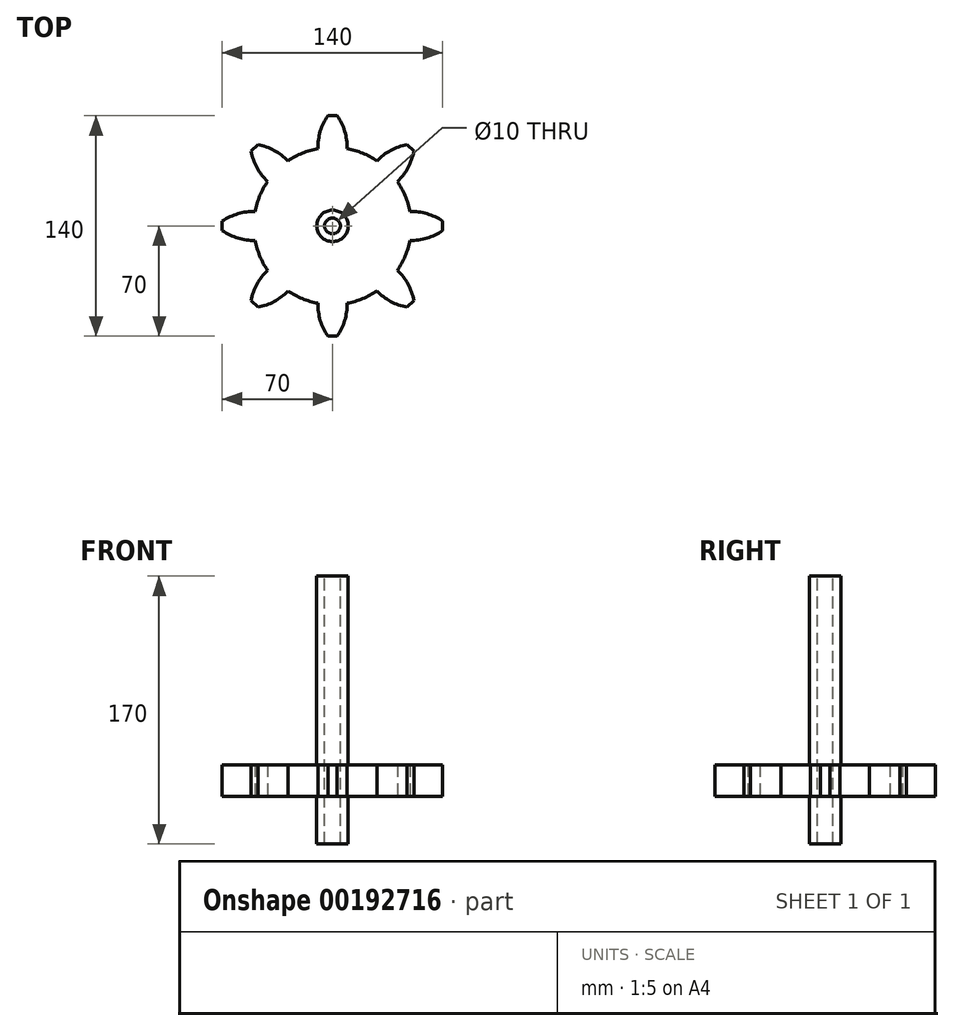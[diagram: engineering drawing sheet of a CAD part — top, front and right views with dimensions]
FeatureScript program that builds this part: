
annotation { "Feature Type Name" : "Feature", "Feature Type Description" : "" }
export const myFeature = defineFeature(function(context is Context, id is Id, definition is map)
    precondition{}
    {
        {
            var Q0;
            Q0=qCreatedBy(makeId("Top.planeOp"),FACE);
            var sketch = newSketch(context, id + "F0", { "sketchPlane" : qUnion([Q0])});
            skCircle(sketch, "E0", {"center": v(0, 0) * mm, "radius": 50 * mm});
            skLineSegment(sketch, "E1", {"start": v(0, 0) * mm, "end": v(0, 50) * mm, "construction": true});
            skLineSegment(sketch, "E2", {"start": v(0, 50) * mm, "end": v(0, 70) * mm});
            skLineSegment(sketch, "E3", {"start": v(0, 70) * mm, "end": v(-3, 70) * mm});
            skArc(sketch, "E4", {"start": v(-3, 70) * mm, "mid": v(-7.76, 60.06) * mm, "end": v(-9.22, 49.14) * mm});
            skLineSegment(sketch, "E5.MirrorCS", {"start": v(0, 70) * mm, "end": v(3, 70) * mm});
            skArc(sketch, "E6.MirrorCS", {"start": v(3, 70) * mm, "mid": v(7.76, 60.06) * mm, "end": v(9.22, 49.14) * mm});
            skArc(sketch, "E7.1.0", {"start": v(-51.62, 47.38) * mm, "mid": v(-47.96, 36.98) * mm, "end": v(-41.27, 28.23) * mm});
            skLineSegment(sketch, "E7.1.1", {"start": v(-49.5, 49.5) * mm, "end": v(-51.62, 47.38) * mm});
            skLineSegment(sketch, "E7.1.2", {"start": v(-49.5, 49.5) * mm, "end": v(-47.38, 51.62) * mm});
            skArc(sketch, "E7.1.3", {"start": v(-47.38, 51.62) * mm, "mid": v(-36.98, 47.96) * mm, "end": v(-28.23, 41.27) * mm});
            skArc(sketch, "E7.2.0", {"start": v(-70, -3) * mm, "mid": v(-60.06, -7.76) * mm, "end": v(-49.14, -9.22) * mm});
            skLineSegment(sketch, "E7.2.1", {"start": v(-70, 0) * mm, "end": v(-70, -3) * mm});
            skLineSegment(sketch, "E7.2.2", {"start": v(-70, 0) * mm, "end": v(-70, 3) * mm});
            skArc(sketch, "E7.2.3", {"start": v(-70, 3) * mm, "mid": v(-60.06, 7.76) * mm, "end": v(-49.14, 9.22) * mm});
            skArc(sketch, "E7.3.0", {"start": v(-47.38, -51.62) * mm, "mid": v(-36.98, -47.96) * mm, "end": v(-28.23, -41.27) * mm});
            skLineSegment(sketch, "E7.3.1", {"start": v(-49.5, -49.5) * mm, "end": v(-47.38, -51.62) * mm});
            skLineSegment(sketch, "E7.3.2", {"start": v(-49.5, -49.5) * mm, "end": v(-51.62, -47.38) * mm});
            skArc(sketch, "E7.3.3", {"start": v(-51.62, -47.38) * mm, "mid": v(-47.96, -36.98) * mm, "end": v(-41.27, -28.23) * mm});
            skArc(sketch, "E7.4.0", {"start": v(3, -70) * mm, "mid": v(7.76, -60.06) * mm, "end": v(9.22, -49.14) * mm});
            skLineSegment(sketch, "E7.4.1", {"start": v(0, -70) * mm, "end": v(3, -70) * mm});
            skLineSegment(sketch, "E7.4.2", {"start": v(0, -70) * mm, "end": v(-3, -70) * mm});
            skArc(sketch, "E7.4.3", {"start": v(-3, -70) * mm, "mid": v(-7.76, -60.06) * mm, "end": v(-9.22, -49.14) * mm});
            skArc(sketch, "E7.5.0", {"start": v(51.62, -47.38) * mm, "mid": v(47.96, -36.98) * mm, "end": v(41.27, -28.23) * mm});
            skLineSegment(sketch, "E7.5.1", {"start": v(49.5, -49.5) * mm, "end": v(51.62, -47.38) * mm});
            skLineSegment(sketch, "E7.5.2", {"start": v(49.5, -49.5) * mm, "end": v(47.38, -51.62) * mm});
            skArc(sketch, "E7.5.3", {"start": v(47.38, -51.62) * mm, "mid": v(36.98, -47.96) * mm, "end": v(28.23, -41.27) * mm});
            skArc(sketch, "E7.6.0", {"start": v(70, 3) * mm, "mid": v(60.06, 7.76) * mm, "end": v(49.14, 9.22) * mm});
            skLineSegment(sketch, "E7.6.1", {"start": v(70, 0) * mm, "end": v(70, 3) * mm});
            skLineSegment(sketch, "E7.6.2", {"start": v(70, 0) * mm, "end": v(70, -3) * mm});
            skArc(sketch, "E7.6.3", {"start": v(70, -3) * mm, "mid": v(60.06, -7.76) * mm, "end": v(49.14, -9.22) * mm});
            skArc(sketch, "E7.7.0", {"start": v(47.38, 51.62) * mm, "mid": v(36.98, 47.96) * mm, "end": v(28.23, 41.27) * mm});
            skLineSegment(sketch, "E7.7.1", {"start": v(49.5, 49.5) * mm, "end": v(47.38, 51.62) * mm});
            skLineSegment(sketch, "E7.7.2", {"start": v(49.5, 49.5) * mm, "end": v(51.62, 47.38) * mm});
            skArc(sketch, "E7.7.3", {"start": v(51.62, 47.38) * mm, "mid": v(47.96, 36.98) * mm, "end": v(41.27, 28.23) * mm});
            skSolve(sketch);
        }
        {
            var Q0;
            Q0 = qSketchRegion(id + "F0", true);
            extrude(context, id + "F1", {"entities" : qUnion([Q0]), "depth" : 20 * mm});
        }
        {
            var Q0;
            Q0=makeQuery(id+"F1.opExtrude","CAP_FACE",FACE,{"disambiguationData":[OSD([sQuery(id+"F0.wireOp",EDGE,"E0"),sQuery(id+"F0.wireOp",EDGE,"E3"),sQuery(id+"F0.wireOp",EDGE,"E4"),sQuery(id+"F0.wireOp",EDGE,"E5.MirrorCS"),sQuery(id+"F0.wireOp",EDGE,"E6.MirrorCS"),sQuery(id+"F0.wireOp",EDGE,"E7.1.0"),sQuery(id+"F0.wireOp",EDGE,"E7.1.1"),sQuery(id+"F0.wireOp",EDGE,"E7.1.2"),sQuery(id+"F0.wireOp",EDGE,"E7.1.3"),sQuery(id+"F0.wireOp",EDGE,"E7.2.0"),sQuery(id+"F0.wireOp",EDGE,"E7.2.1"),sQuery(id+"F0.wireOp",EDGE,"E7.2.2"),sQuery(id+"F0.wireOp",EDGE,"E7.2.3"),sQuery(id+"F0.wireOp",EDGE,"E7.3.0"),sQuery(id+"F0.wireOp",EDGE,"E7.3.1"),sQuery(id+"F0.wireOp",EDGE,"E7.3.2"),sQuery(id+"F0.wireOp",EDGE,"E7.3.3"),sQuery(id+"F0.wireOp",EDGE,"E7.4.0"),sQuery(id+"F0.wireOp",EDGE,"E7.4.1"),sQuery(id+"F0.wireOp",EDGE,"E7.4.2"),sQuery(id+"F0.wireOp",EDGE,"E7.4.3"),sQuery(id+"F0.wireOp",EDGE,"E7.5.0"),sQuery(id+"F0.wireOp",EDGE,"E7.5.1"),sQuery(id+"F0.wireOp",EDGE,"E7.5.2"),sQuery(id+"F0.wireOp",EDGE,"E7.5.3"),sQuery(id+"F0.wireOp",EDGE,"E7.6.0"),sQuery(id+"F0.wireOp",EDGE,"E7.6.1"),sQuery(id+"F0.wireOp",EDGE,"E7.6.2"),sQuery(id+"F0.wireOp",EDGE,"E7.6.3"),sQuery(id+"F0.wireOp",EDGE,"E7.7.0"),sQuery(id+"F0.wireOp",EDGE,"E7.7.1"),sQuery(id+"F0.wireOp",EDGE,"E7.7.2"),sQuery(id+"F0.wireOp",EDGE,"E7.7.3"),sQuery(id+"F0.wireOp",EDGE,"E7.8.0"),sQuery(id+"F0.wireOp",EDGE,"E7.8.1"),sQuery(id+"F0.wireOp",EDGE,"E7.8.2"),sQuery(id+"F0.wireOp",EDGE,"E7.8.3"),sQuery(id+"F0.wireOp",EDGE,"E7.9.0"),sQuery(id+"F0.wireOp",EDGE,"E7.9.1"),sQuery(id+"F0.wireOp",EDGE,"E7.9.2"),sQuery(id+"F0.wireOp",EDGE,"E7.9.3"),sQuery(id+"F0.wireOp",EDGE,"E7.10.0"),sQuery(id+"F0.wireOp",EDGE,"E7.10.1"),sQuery(id+"F0.wireOp",EDGE,"E7.10.2"),sQuery(id+"F0.wireOp",EDGE,"E7.10.3"),sQuery(id+"F0.wireOp",EDGE,"E7.11.0"),sQuery(id+"F0.wireOp",EDGE,"E7.11.1"),sQuery(id+"F0.wireOp",EDGE,"E7.11.2"),sQuery(id+"F0.wireOp",EDGE,"E7.11.3"),sQuery(id+"F0.wireOp",EDGE,"E7.12.0"),sQuery(id+"F0.wireOp",EDGE,"E7.12.1"),sQuery(id+"F0.wireOp",EDGE,"E7.12.2"),sQuery(id+"F0.wireOp",EDGE,"E7.12.3"),sQuery(id+"F0.wireOp",EDGE,"E7.13.0"),sQuery(id+"F0.wireOp",EDGE,"E7.13.1"),sQuery(id+"F0.wireOp",EDGE,"E7.13.2"),sQuery(id+"F0.wireOp",EDGE,"E7.13.3"),sQuery(id+"F0.wireOp",EDGE,"E7.14.0"),sQuery(id+"F0.wireOp",EDGE,"E7.14.1"),sQuery(id+"F0.wireOp",EDGE,"E7.14.2"),sQuery(id+"F0.wireOp",EDGE,"E7.14.3"),sQuery(id+"F0.wireOp",EDGE,"E7.15.0"),sQuery(id+"F0.wireOp",EDGE,"E7.15.1"),sQuery(id+"F0.wireOp",EDGE,"E7.15.2"),sQuery(id+"F0.wireOp",EDGE,"E7.15.3")])],"isStart":false});
            var sketch = newSketch(context, id + "F2", { "sketchPlane" : qUnion([Q0])});
            skCircle(sketch, "E8", {"center": v(0, 0) * mm, "radius": 10 * mm});
            skSolve(sketch);
        }
        {
            var Q0;
            Q0 = qSketchRegion(id + "F2", true);
            extrude(context, id + "F3", {"entities" : qUnion([Q0]), "operationType" : NewBodyOperationType.ADD, "depth" : 120 * mm, "hasSecondDirection" : true, "secondDirectionOppositeDirection" : true, "secondDirectionDepth" : 50 * mm});
        }
        {
            var Q0;
            Q0=makeQuery(id+"F3.opExtrude","CAP_FACE",FACE,{"disambiguationData":[OSD([sQuery(id+"F2.wireOp",EDGE,"E8")])],"isStart":false});
            var sketch = newSketch(context, id + "F4", { "sketchPlane" : qUnion([Q0])});
            skCircle(sketch, "E9", {"center": v(0, 0) * mm, "radius": 5 * mm});
            skSolve(sketch);
        }
        {
            var Q0;
            Q0 = qSketchRegion(id + "F4", true);
            extrude(context, id + "F5", {"entities" : qUnion([Q0]), "operationType" : NewBodyOperationType.REMOVE, "endBound" : BoundingType.UP_TO_NEXT, "oppositeDirection" : true, "depth" : 25 * mm});
        }
    });
